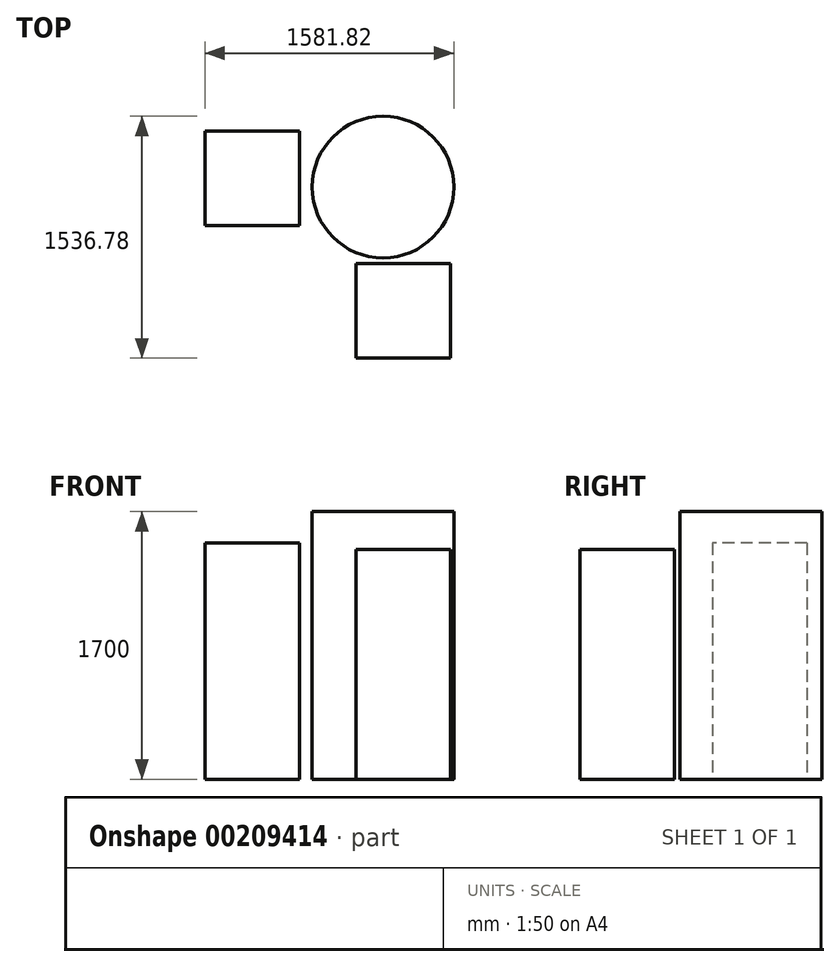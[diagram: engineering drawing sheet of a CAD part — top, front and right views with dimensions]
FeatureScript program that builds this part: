
annotation { "Feature Type Name" : "Feature", "Feature Type Description" : "" }
export const myFeature = defineFeature(function(context is Context, id is Id, definition is map)
    precondition{}
    {
        {
            var Q0;
            Q0=qCreatedBy(makeId("Top.planeOp"),FACE);
            var sketch = newSketch(context, id + "F0", { "sketchPlane" : qUnion([Q0])});
            skLineSegment(sketch, "E0", {"start": v(0, 0) * mm, "end": v(2350, 0) * mm});
            skLineSegment(sketch, "E1", {"start": v(2350, 0) * mm, "end": v(2350, -4350) * mm});
            skLineSegment(sketch, "E2", {"start": v(2350, -4350) * mm, "end": v(-1600, -4350) * mm});
            skLineSegment(sketch, "E3", {"start": v(-1600, -4350) * mm, "end": v(-1600, -410) * mm});
            skLineSegment(sketch, "E4", {"start": v(-1600, -410) * mm, "end": v(0, -410) * mm});
            skLineSegment(sketch, "E5", {"start": v(0, -410) * mm, "end": v(0, 0) * mm});
            skLineSegment(sketch, "E6", {"start": v(-1600, -410) * mm, "end": v(-1880, -410) * mm});
            skLineSegment(sketch, "E7", {"start": v(-1880, -410) * mm, "end": v(-1880, -2840) * mm});
            skLineSegment(sketch, "E8", {"start": v(-1600, -4350) * mm, "end": v(-1880, -4350) * mm});
            skLineSegment(sketch, "E9", {"start": v(-1880, -4350) * mm, "end": v(-1880, -3750) * mm});
            skLineSegment(sketch, "E10", {"start": v(-1880, -3750) * mm, "end": v(-1600, -3750) * mm});
            skLineSegment(sketch, "E11", {"start": v(-1880, -2840) * mm, "end": v(-1600, -2840) * mm});
            skSolve(sketch);
        }
        {
            var Q0;
            Q0=qCreatedBy(makeId("Top.planeOp"),FACE);
            var sketch = newSketch(context, id + "F1", { "sketchPlane" : qUnion([Q0])});
            skCircle(sketch, "E12", {"center": v(1898.9, -471.44) * mm, "radius": 450 * mm});
            skLineSegment(sketch, "E13.bottom", {"start": v(1727.82, -958.22) * mm, "end": v(2327.82, -958.22) * mm});
            skLineSegment(sketch, "E13.top", {"start": v(1727.82, -1558.22) * mm, "end": v(2327.82, -1558.22) * mm});
            skLineSegment(sketch, "E13.left", {"start": v(1727.82, -958.22) * mm, "end": v(1727.82, -1558.22) * mm});
            skLineSegment(sketch, "E13.right", {"start": v(2327.82, -958.22) * mm, "end": v(2327.82, -1558.22) * mm});
            skSolve(sketch);
        }
        {
            var Q0;
            Q0=makeQuery(id+"F0.imprint","IMPRINT",FACE,{"disambiguationData":[TD([[makeQuery(id+"F0.imprint","IMPRINT",EDGE,{"derivedFrom":sQuery(id+"F0.wireOp",EDGE,"E0")}),-1.0]])]});
            var sketch = newSketch(context, id + "F2", { "sketchPlane" : qUnion([Q0])});
            skSolve(sketch);
        }
        {
            var Q0;
            Q0=makeQuery(id+"F2.imprint","IMPRINT",FACE,{"disambiguationData":[TD([[makeQuery(id+"F2.imprint","IMPRINT",EDGE,{"derivedFrom":makeQuery(id+"F0.imprint","IMPRINT",EDGE,{"derivedFrom":sQuery(id+"F0.wireOp",EDGE,"E0")})}),-1.0]])]});
            var sketch = newSketch(context, id + "F3", { "sketchPlane" : qUnion([Q0])});
            skLineSegment(sketch, "E14.bottom", {"start": v(767.08, -116.12) * mm, "end": v(1367.08, -116.12) * mm});
            skLineSegment(sketch, "E14.top", {"start": v(767.08, -716.12) * mm, "end": v(1367.08, -716.12) * mm});
            skLineSegment(sketch, "E14.left", {"start": v(767.08, -116.12) * mm, "end": v(767.08, -716.12) * mm});
            skLineSegment(sketch, "E14.right", {"start": v(1367.08, -116.12) * mm, "end": v(1367.08, -716.12) * mm});
            skSolve(sketch);
        }
        {
            var Q0;
            Q0 = qSketchRegion(id + "F3", true);
            extrude(context, id + "F4", {"entities" : qUnion([Q0]), "depth" : 1500 * mm});
        }
        {
            var Q0;
            Q0=makeQuery(id+"F1.imprint","IMPRINT",FACE,{"disambiguationData":[TD([[makeQuery(id+"F1.imprint","IMPRINT",EDGE,{"derivedFrom":sQuery(id+"F1.wireOp",EDGE,"E12")}),1.0]])]});
            extrude(context, id + "F5", {"entities" : qUnion([Q0]), "depth" : 1700 * mm});
        }
        {
            var Q0;
            Q0 = qSketchRegion(id + "F1", true);
            extrude(context, id + "F6", {"entities" : qUnion([Q0]), "operationType" : NewBodyOperationType.ADD, "depth" : 1460 * mm});
        }
    });
